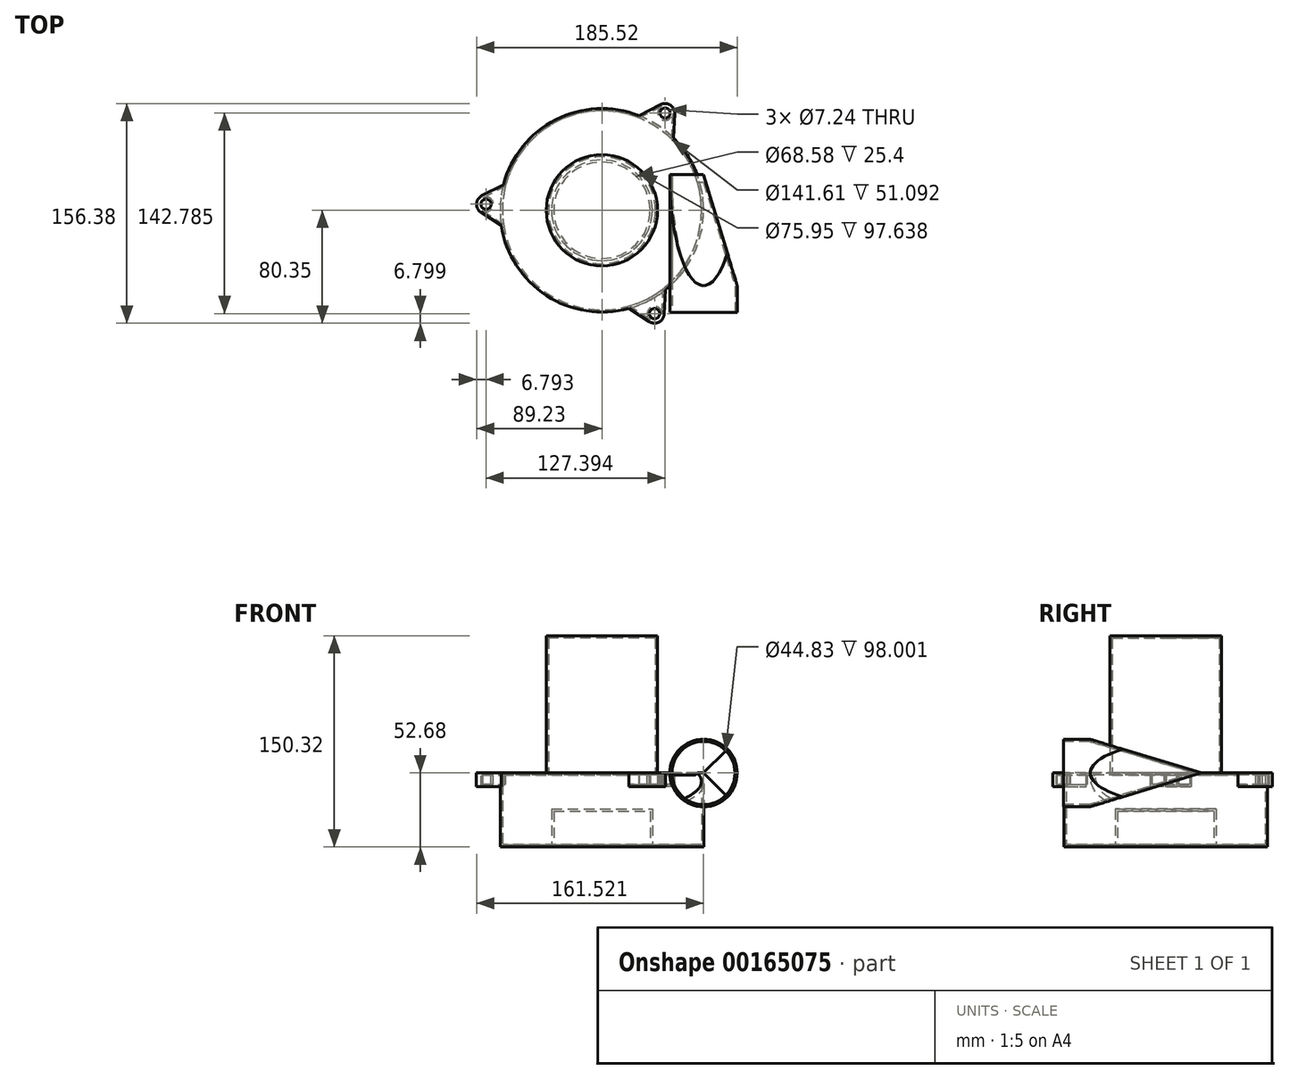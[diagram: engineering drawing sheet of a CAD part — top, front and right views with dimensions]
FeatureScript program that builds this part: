
annotation { "Feature Type Name" : "Feature", "Feature Type Description" : "" }
export const myFeature = defineFeature(function(context is Context, id is Id, definition is map)
    precondition{}
    {
        {
            var Q0;
            Q0=qCreatedBy(makeId("Top.planeOp"),FACE);
            var sketch = newSketch(context, id + "F0", { "sketchPlane" : qUnion([Q0])});
            skCircle(sketch, "E0", {"center": v(0, 0) * mm, "radius": 72.4 * mm});
            skSolve(sketch);
        }
        {
            var Q0;
            Q0 = qSketchRegion(id + "F0", true);
            extrude(context, id + "F1", {"entities" : qUnion([Q0]), "depth" : 52.68 * mm});
        }
        {
            var Q0;
            Q0=makeQuery(id+"F1.opExtrude","CAP_FACE",FACE,{"disambiguationData":[OSD([sQuery(id+"F0.wireOp",EDGE,"E0")])],"isStart":false});
            var sketch = newSketch(context, id + "F2", { "sketchPlane" : qUnion([Q0])});
            skLineSegment(sketch, "E1", {"start": v(0, 0) * mm, "end": v(37.48, -73.55) * mm, "construction": true});
            skLineSegment(sketch, "E2", {"start": v(0, 0) * mm, "end": v(-82.44, 4.32) * mm, "construction": true});
            skLineSegment(sketch, "E3", {"start": v(-82.44, 4.32) * mm, "end": v(37.48, -73.55) * mm, "construction": true});
            skLineSegment(sketch, "E4", {"start": v(37.48, -73.55) * mm, "end": v(44.96, 69.23) * mm, "construction": true});
            skLineSegment(sketch, "E5", {"start": v(44.96, 69.23) * mm, "end": v(0, 0) * mm, "construction": true});
            skLineSegment(sketch, "E6", {"start": v(-82.44, 4.32) * mm, "end": v(44.96, 69.23) * mm, "construction": true});
            skCircle(sketch, "E7", {"center": v(-82.44, 4.32) * mm, "radius": 3.62 * mm});
            skCircle(sketch, "E8", {"center": v(44.96, 69.23) * mm, "radius": 3.62 * mm});
            skCircle(sketch, "E9", {"center": v(37.48, -73.55) * mm, "radius": 3.62 * mm});
            skArc(sketch, "E10", {"start": v(-85.52, 10.37) * mm, "mid": v(-89.22, 4.67) * mm, "end": v(-86.14, -1.38) * mm});
            skArc(sketch, "E11", {"start": v(51.74, 68.88) * mm, "mid": v(48.66, 74.93) * mm, "end": v(41.87, 75.29) * mm});
            skArc(sketch, "E12", {"start": v(33.78, -79.25) * mm, "mid": v(40.57, -79.6) * mm, "end": v(44.27, -73.9) * mm});
            skLineSegment(sketch, "E13", {"start": v(-86.14, -1.38) * mm, "end": v(-71.57, -10.84) * mm});
            skLineSegment(sketch, "E14", {"start": v(-85.52, 10.37) * mm, "end": v(-70.05, 18.25) * mm});
            skLineSegment(sketch, "E15", {"start": v(41.87, 75.29) * mm, "end": v(26.4, 67.4) * mm});
            skLineSegment(sketch, "E16", {"start": v(51.74, 68.88) * mm, "end": v(50.83, 51.54) * mm});
            skLineSegment(sketch, "E17", {"start": v(44.27, -73.9) * mm, "end": v(45.17, -56.57) * mm});
            skLineSegment(sketch, "E18", {"start": v(33.78, -79.25) * mm, "end": v(19.22, -69.8) * mm});
            skArc(sketch, "E19", {"start": v(-70.05, 18.25) * mm, "mid": v(-72.3, 3.79) * mm, "end": v(-71.57, -10.84) * mm});
            skLineSegment(sketch, "E20", {"start": v(-86.14, -1.38) * mm, "end": v(-78.63, -1.78) * mm, "construction": true});
            skLineSegment(sketch, "E21", {"start": v(-78.63, -1.78) * mm, "end": v(-78.86, -6.11) * mm, "construction": true});
            skArc(sketch, "E22", {"start": v(50.83, 51.54) * mm, "mid": v(39.42, 60.71) * mm, "end": v(26.4, 67.4) * mm});
            skArc(sketch, "E23", {"start": v(19.22, -69.8) * mm, "mid": v(32.87, -64.5) * mm, "end": v(45.17, -56.57) * mm});
            skLineSegment(sketch, "E24", {"start": v(0, 0) * mm, "end": v(72.4, 0) * mm, "construction": true});
            skLineSegment(sketch, "E25", {"start": v(72.4, 0) * mm, "end": v(72.4, -72.9) * mm, "construction": true});
            skLineSegment(sketch, "E26.bottom", {"start": v(96.4, -72.9) * mm, "end": v(48.39, -72.9) * mm, "construction": true});
            skLineSegment(sketch, "E26.top", {"start": v(96.4, -53.84) * mm, "end": v(48.39, -53.84) * mm, "construction": true});
            skLineSegment(sketch, "E26.left", {"start": v(96.4, -72.9) * mm, "end": v(96.4, -53.84) * mm, "construction": true});
            skLineSegment(sketch, "E26.right", {"start": v(48.39, -72.9) * mm, "end": v(48.39, -53.84) * mm, "construction": true});
            skSolve(sketch);
        }
        {
            var Q0;
            Q0 = qSketchRegion(id + "F2", true);
            extrude(context, id + "F3", {"entities" : qUnion([Q0]), "operationType" : NewBodyOperationType.ADD, "oppositeDirection" : true, "depth" : 9.65 * mm});
        }
        {
            var Q0;
            Q0=makeQuery(id+"F1.opExtrude","CAP_FACE",FACE,{"disambiguationData":[OSD([sQuery(id+"F0.wireOp",EDGE,"E0")])],"isStart":true});
            var sketch = newSketch(context, id + "F4", { "sketchPlane" : qUnion([Q0])});
            skCircle(sketch, "E27", {"center": v(0, 0) * mm, "radius": 34.3 * mm});
            skSolve(sketch);
        }
        {
            var Q0;
            Q0 = qSketchRegion(id + "F4", true);
            extrude(context, id + "F5", {"entities" : qUnion([Q0]), "operationType" : NewBodyOperationType.REMOVE, "oppositeDirection" : true, "depth" : 25.4 * mm});
        }
        {
            var Q0;
            Q0=makeQuery(id+"F3.boolean.opBoolean","MERGE",FACE,{"derivedFrom":[makeQuery(id+"F1.opExtrude","CAP_FACE",FACE,{"disambiguationData":[OSD([sQuery(id+"F0.wireOp",EDGE,"E0")])],"isStart":false}),makeQuery(id+"F3.opExtrude","CAP_FACE",FACE,{"disambiguationData":[OSD([sQuery(id+"F2.wireOp",EDGE,"E7"),sQuery(id+"F2.wireOp",EDGE,"E10"),sQuery(id+"F2.wireOp",EDGE,"E13"),sQuery(id+"F2.wireOp",EDGE,"E14"),sQuery(id+"F2.wireOp",EDGE,"E19")])],"isStart":true}),makeQuery(id+"F3.opExtrude","CAP_FACE",FACE,{"disambiguationData":[OSD([sQuery(id+"F2.wireOp",EDGE,"E8"),sQuery(id+"F2.wireOp",EDGE,"E11"),sQuery(id+"F2.wireOp",EDGE,"E15"),sQuery(id+"F2.wireOp",EDGE,"E16"),sQuery(id+"F2.wireOp",EDGE,"E22")])],"isStart":true}),makeQuery(id+"F3.opExtrude","CAP_FACE",FACE,{"disambiguationData":[OSD([sQuery(id+"F2.wireOp",EDGE,"E9"),sQuery(id+"F2.wireOp",EDGE,"E12"),sQuery(id+"F2.wireOp",EDGE,"E17"),sQuery(id+"F2.wireOp",EDGE,"E18"),sQuery(id+"F2.wireOp",EDGE,"E23")])],"isStart":true})]});
            var sketch = newSketch(context, id + "F6", { "sketchPlane" : qUnion([Q0])});
            skCircle(sketch, "E28", {"center": v(0, 0) * mm, "radius": 39.56 * mm});
            skSolve(sketch);
        }
        {
            var Q0;
            Q0 = qSketchRegion(id + "F6", true);
            extrude(context, id + "F7", {"entities" : qUnion([Q0]), "operationType" : NewBodyOperationType.ADD, "depth" : 97.64 * mm});
        }
        {
            var Q0;
            Q0=qCreatedBy(makeId("Front.planeOp"),FACE);
            var sketch = newSketch(context, id + "F8", { "sketchPlane" : qUnion([Q0])});
            skCircle(sketch, "E29", {"center": v(72.3, 52.68) * mm, "radius": 24 * mm, "construction": true});
            skLineSegment(sketch, "E30.bottom", {"start": v(96.3, 76.68) * mm, "end": v(48.29, 76.68) * mm});
            skLineSegment(sketch, "E30.top", {"start": v(96.3, 28.68) * mm, "end": v(48.29, 28.68) * mm});
            skLineSegment(sketch, "E30.left", {"start": v(96.3, 76.68) * mm, "end": v(96.3, 28.68) * mm});
            skLineSegment(sketch, "E30.right", {"start": v(48.29, 76.68) * mm, "end": v(48.29, 28.68) * mm});
            skSolve(sketch);
        }
        {
            var Q0;
            Q0 = qSketchRegion(id + "F8", true);
            extrude(context, id + "F9", {"entities" : qUnion([Q0]), "operationType" : NewBodyOperationType.ADD, "depth" : 72.84 * mm, "hasSecondDirection" : true, "secondDirectionOppositeDirection" : true, "secondDirectionDepth" : 25.4 * mm});
        }
        {
            var Q0;
            Q0=makeQuery(id+"F9.opExtrude","SWEPT_FACE",FACE,{"disambiguationData":[OSD([sQuery(id+"F8.wireOp",EDGE,"E30.left")])]});
            var sketch = newSketch(context, id + "F10", { "sketchPlane" : qUnion([Q0])});
            skLineSegment(sketch, "E31.bottom", {"start": v(25.4, 52.68) * mm, "end": v(-53.79, 52.68) * mm, "construction": true});
            skLineSegment(sketch, "E31.top", {"start": v(25.4, 28.68) * mm, "end": v(-53.79, 28.68) * mm});
            skLineSegment(sketch, "E31.left", {"start": v(25.4, 52.68) * mm, "end": v(25.4, 28.68) * mm});
            skLineSegment(sketch, "E31.right", {"start": v(-53.79, 52.68) * mm, "end": v(-53.79, 28.68) * mm, "construction": true});
            skLineSegment(sketch, "E32", {"start": v(25.4, 52.68) * mm, "end": v(-53.79, 28.68) * mm});
            skSolve(sketch);
        }
        {
            var Q0;
            Q0 = qSketchRegion(id + "F10", true);
            var Q1;
            Q1=makeQuery(id+"F1.opExtrude","SWEPT_FACE",FACE,{"disambiguationData":[OSD([sQuery(id+"F0.wireOp",EDGE,"E0")])]});
            extrude(context, id + "F11", {"entities" : qUnion([Q0]), "operationType" : NewBodyOperationType.REMOVE, "endBound" : BoundingType.UP_TO_SURFACE, "oppositeDirection" : true, "endBoundEntityFace" : qUnion([Q1]), "depth" : 25.4 * mm});
        }
        {
            var Q0;
            Q0=makeQuery(id+"F9.opExtrude","SWEPT_FACE",FACE,{"disambiguationData":[OSD([sQuery(id+"F8.wireOp",EDGE,"E30.right")])]});
            var sketch = newSketch(context, id + "F12", { "sketchPlane" : qUnion([Q0])});
            skLineSegment(sketch, "E33.bottom", {"start": v(-25.4, 52.68) * mm, "end": v(53.79, 52.68) * mm, "construction": true});
            skLineSegment(sketch, "E33.top", {"start": v(-25.4, 76.68) * mm, "end": v(53.79, 76.68) * mm});
            skLineSegment(sketch, "E33.left", {"start": v(-25.4, 52.68) * mm, "end": v(-25.4, 76.68) * mm});
            skLineSegment(sketch, "E33.right", {"start": v(53.79, 52.68) * mm, "end": v(53.79, 76.68) * mm, "construction": true});
            skLineSegment(sketch, "E34", {"start": v(53.79, 52.68) * mm, "end": v(53.79, 28.68) * mm, "construction": true});
            skLineSegment(sketch, "E35", {"start": v(53.79, 76.68) * mm, "end": v(-25.4, 52.68) * mm});
            skSolve(sketch);
        }
        {
            var Q0;
            Q0 = qSketchRegion(id + "F12", true);
            var Q1;
            Q1=makeQuery(id+"F9.opExtrude","SWEPT_FACE",FACE,{"disambiguationData":[OSD([sQuery(id+"F8.wireOp",EDGE,"E30.left")])]});
            extrude(context, id + "F13", {"entities" : qUnion([Q0]), "operationType" : NewBodyOperationType.REMOVE, "endBound" : BoundingType.UP_TO_SURFACE, "oppositeDirection" : true, "endBoundEntityFace" : qUnion([Q1]), "depth" : 25.4 * mm});
        }
        {
            var Q0;
            Q0=makeQuery(id+"F9.opExtrude","SWEPT_EDGE",EDGE,{"disambiguationData":[OSD([sQuery(id+"F8.wireOp",EDGE,"E30.bottom"),sQuery(id+"F8.wireOp",EDGE,"E30.left")])]});
            var Q1;
            Q1=makeQuery(id+"F9.opExtrude","SWEPT_EDGE",EDGE,{"disambiguationData":[OSD([sQuery(id+"F8.wireOp",EDGE,"E30.bottom"),sQuery(id+"F8.wireOp",EDGE,"E30.right")])]});
            var Q2;
            Q2=makeQuery(id+"F9.opExtrude","SWEPT_EDGE",EDGE,{"disambiguationData":[OSD([sQuery(id+"F8.wireOp",EDGE,"E30.top"),sQuery(id+"F8.wireOp",EDGE,"E30.left")])]});
            var Q3;
            Q3=makeQuery(id+"F9.opExtrude","SWEPT_EDGE",EDGE,{"disambiguationData":[OSD([sQuery(id+"F8.wireOp",EDGE,"E30.top"),sQuery(id+"F8.wireOp",EDGE,"E30.right")])]});
            fillet(context, id + "F14", {"entities" : qUnion([Q0, Q1, Q2, Q3]), "radius" : 24 * mm, "tangentPropagation" : true, "allowEdgeOverflow" : false});
        }
        {
            var Q0;
            Q0=makeQuery(id+"F3.boolean.opBoolean","MERGE",FACE,{"derivedFrom":[makeQuery(id+"F1.opExtrude","CAP_FACE",FACE,{"disambiguationData":[OSD([sQuery(id+"F0.wireOp",EDGE,"E0")])],"isStart":false}),makeQuery(id+"F3.opExtrude","CAP_FACE",FACE,{"disambiguationData":[OSD([sQuery(id+"F2.wireOp",EDGE,"E7"),sQuery(id+"F2.wireOp",EDGE,"E10"),sQuery(id+"F2.wireOp",EDGE,"E13"),sQuery(id+"F2.wireOp",EDGE,"E14"),sQuery(id+"F2.wireOp",EDGE,"E19")])],"isStart":true}),makeQuery(id+"F3.opExtrude","CAP_FACE",FACE,{"disambiguationData":[OSD([sQuery(id+"F2.wireOp",EDGE,"E8"),sQuery(id+"F2.wireOp",EDGE,"E11"),sQuery(id+"F2.wireOp",EDGE,"E15"),sQuery(id+"F2.wireOp",EDGE,"E16"),sQuery(id+"F2.wireOp",EDGE,"E22")])],"isStart":true}),makeQuery(id+"F3.opExtrude","CAP_FACE",FACE,{"disambiguationData":[OSD([sQuery(id+"F2.wireOp",EDGE,"E9"),sQuery(id+"F2.wireOp",EDGE,"E12"),sQuery(id+"F2.wireOp",EDGE,"E17"),sQuery(id+"F2.wireOp",EDGE,"E18"),sQuery(id+"F2.wireOp",EDGE,"E23")])],"isStart":true})]});
            var sketch = newSketch(context, id + "F15", { "sketchPlane" : qUnion([Q0])});
            skLineSegment(sketch, "E36.bottom", {"start": v(72.3, 25.4) * mm, "end": v(96.3, 25.4) * mm});
            skLineSegment(sketch, "E36.top", {"start": v(72.3, -53.79) * mm, "end": v(96.3, -53.79) * mm, "construction": true});
            skLineSegment(sketch, "E36.left", {"start": v(72.3, 25.4) * mm, "end": v(72.3, -53.79) * mm, "construction": true});
            skLineSegment(sketch, "E36.right", {"start": v(96.3, 25.4) * mm, "end": v(96.3, -53.79) * mm});
            skLineSegment(sketch, "E37", {"start": v(96.3, -53.79) * mm, "end": v(72.3, 25.4) * mm});
            skSolve(sketch);
        }
        {
            var Q0;
            Q0 = qSketchRegion(id + "F15", true);
            var Q1;
            Q1=makeQuery(id+"F11.boolean.opBoolean","COPY",FACE,{"derivedFrom":makeQuery(id+"F11.opExtrude","SWEPT_FACE",FACE,{"disambiguationData":[OSD([sQuery(id+"F10.wireOp",EDGE,"E32")])]})});
            var Q2;
            Q2=makeQuery(id+"F13.boolean.opBoolean","COPY",FACE,{"derivedFrom":makeQuery(id+"F13.opExtrude","SWEPT_FACE",FACE,{"disambiguationData":[OSD([sQuery(id+"F12.wireOp",EDGE,"E35")])]})});
            extrude(context, id + "F16", {"entities" : qUnion([Q0]), "operationType" : NewBodyOperationType.REMOVE, "endBound" : BoundingType.UP_TO_SURFACE, "oppositeDirection" : true, "endBoundEntityFace" : qUnion([Q1]), "depth" : 25.4 * mm, "hasSecondDirection" : true, "secondDirectionBound" : SecondDirectionBoundingType.UP_TO_SURFACE, "secondDirectionOppositeDirection" : false, "secondDirectionBoundEntityFace" : qUnion([Q2]), "secondDirectionDepth" : 25.4 * mm});
        }
        {
            var Q0;
            Q0=makeQuery(id+"F9.opExtrude","CAP_FACE",FACE,{"disambiguationData":[OSD([sQuery(id+"F8.wireOp",EDGE,"E30.bottom"),sQuery(id+"F8.wireOp",EDGE,"E30.top"),sQuery(id+"F8.wireOp",EDGE,"E30.left"),sQuery(id+"F8.wireOp",EDGE,"E30.right")])],"isStart":false});
            shell(context, id + "F17", {"entities" : qUnion([Q0]), "thickness" : 1.59 * mm});
        }
    });
